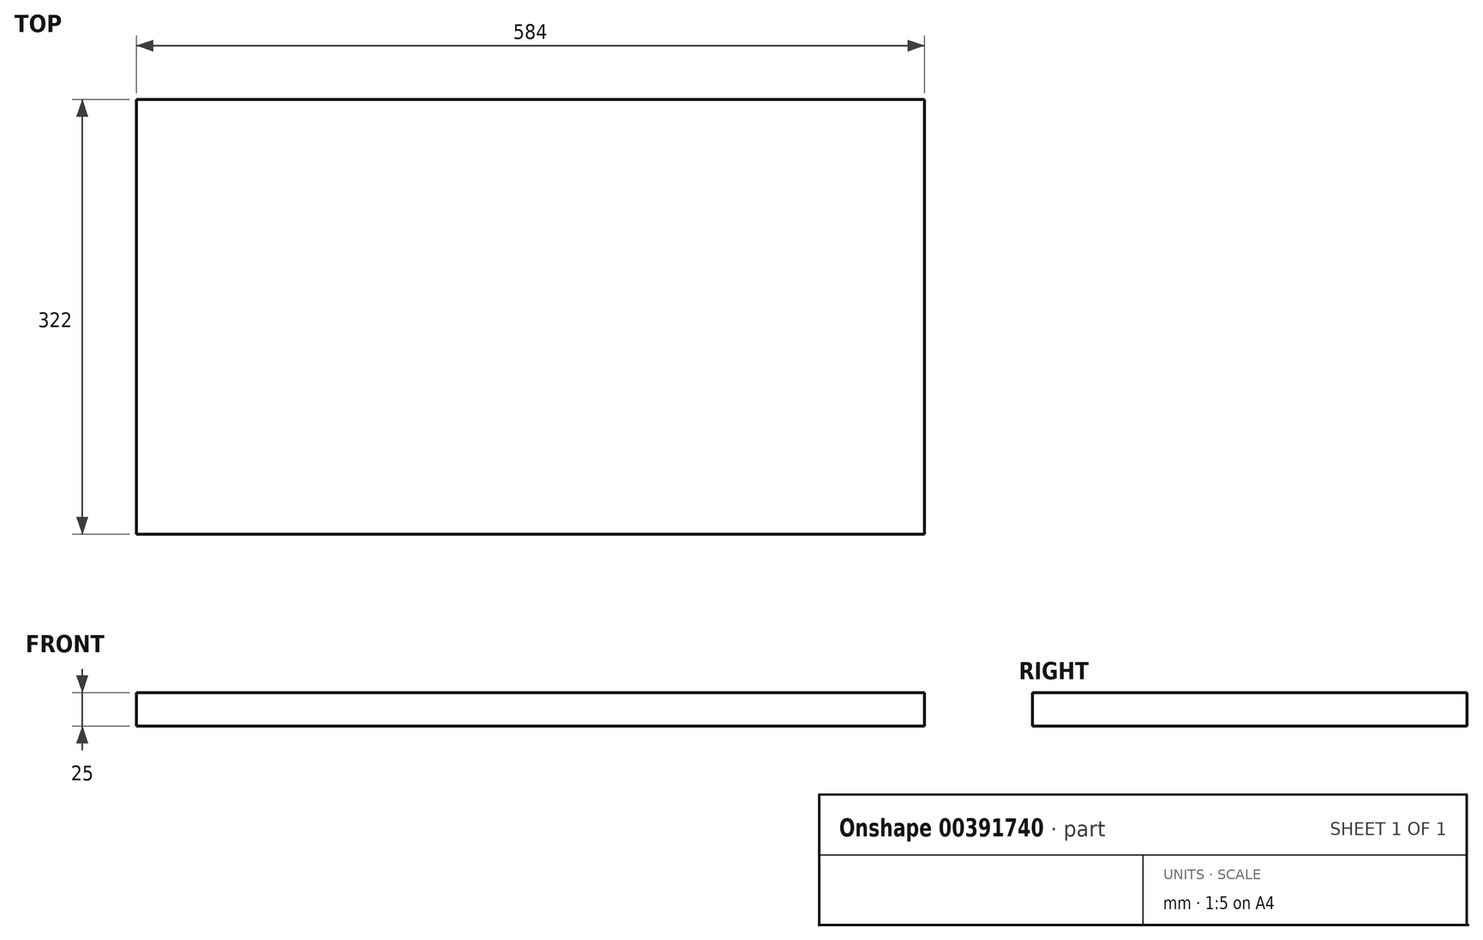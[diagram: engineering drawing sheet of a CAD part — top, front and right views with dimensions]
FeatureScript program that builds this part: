
annotation { "Feature Type Name" : "Feature", "Feature Type Description" : "" }
export const myFeature = defineFeature(function(context is Context, id is Id, definition is map)
    precondition{}
    {
        {
            var Q0;
            Q0=qCreatedBy(makeId("Top.planeOp"),FACE);
            var sketch = newSketch(context, id + "F0", { "sketchPlane" : qUnion([Q0])});
            skLineSegment(sketch, "E0.bottom", {"start": v(292, -161) * mm, "end": v(-292, -161) * mm});
            skLineSegment(sketch, "E0.top", {"start": v(292, 161) * mm, "end": v(-292, 161) * mm});
            skLineSegment(sketch, "E0.left", {"start": v(292, -161) * mm, "end": v(292, 161) * mm});
            skLineSegment(sketch, "E0.right", {"start": v(-292, -161) * mm, "end": v(-292, 161) * mm});
            skPoint(sketch, "E0.middle", {"position": v(0, 0) * mm});
            skSolve(sketch);
        }
        {
            var Q0;
            Q0=makeQuery(id+"F0.imprint","IMPRINT",FACE,{"disambiguationData":[TD([[makeQuery(id+"F0.imprint","IMPRINT",EDGE,{"derivedFrom":sQuery(id+"F0.wireOp",EDGE,"E0.bottom")}),-1.0]])]});
            extrude(context, id + "F1", {"entities" : qUnion([Q0]), "depth" : 25 * mm});
        }
    });
